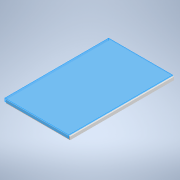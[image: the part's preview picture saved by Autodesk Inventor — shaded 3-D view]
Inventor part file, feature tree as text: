
AUTODESK INVENTOR PART (.ipt)
format: ipt  version: 2021 (Build 250183000, 183)  size: 90,624 bytes
history: native  units: in
note: dims shown in document units (in); Inventor stores cm internally (conversion verified against a paired STEP export)
features: extrude x1, sketch x1
ambient origin geometry x8: Origin, YZ Plane, XZ Plane, XY Plane, X Axis, Y Axis, Z Axis, Center Point
bodies: Solid1 (feature_tree)
feature tree (2):
  extrude  "Extrusion1"  Depth=16.9291in
  sketch  "Sketch1"  dims[d1=10.4331in d2=16.9291in d3=0.5in d4=0.0in]
